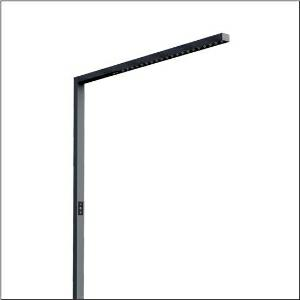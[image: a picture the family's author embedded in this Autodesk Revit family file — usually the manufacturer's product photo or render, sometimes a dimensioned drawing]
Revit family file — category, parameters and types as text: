
# Revit family: silica_31_floor_51my52fatcb
name_source: partatom
category: Lighting Fixtures
units: mm (PartAtom-declared; Revit-internal decimal feet)

## family parameters
Cut with Voids When Loaded = No
Host = Face
Light Source = No
Part Type = Normal
Room Calculation Point = No
Round Connector Dimension = Use Diameter
Shared = No

## types (1)
- --- (1 x LED, 8520 lm, 71 W, 4000K)
    Apparent Load = 71 VA
    CIE Flux Codes = 86 100 100 24 100
    Color Rendering = 80
    Color Temperature = 4000K
    Default Elevation = 1800 mm
    Description = Silica® 31 Floor, floorstanding luminaire, secondary optical cover: cover panel, of PMMA, light emission: direct/indirect distribution, primary light characteristic: symmetric, installation type: not mounted, LED, rated luminous flux: 8.520lm, luminous efficacy: 120lm/W, light colour: 8tw, colour temperature: 2700..6500K, control gear: Touchdim, daylight-dependent control, with cable with plug, mains connection: 230V, AC, 50Hz, connection cable included, cable length: 2,5m, rated input power: 71W, luminaire head, of aluminium, jet black (RAL 9005), length: 1.203mm, width: 52mm, supporting column, angular, of aluminium, jet black (RAL 9005), baseplate, of steel, jet black (RAL 9005), local control - self-sufficient standalone sensors, direct and indirect component separately switchable, protection rating (complete): IP20, insulation class (complete): insulation class I (protective earthing), certification: CE, ENEC, permissible operating ambient temperature: -20..+40°C, standard: EN 50419, packaging unit: 1 piece
    Height = 36 mm
    Lamp = 1 x LED
    Lamp Light Flux = 8520 lm
    Lamp Power = 71 W
    Lamp count = 1
    Length = 1203 mm
    Luminous efficacy = 120 lm/W
    Manufacturer = Siteco
    ModVariant = No
    Model = 51MY52FATCB
    Mounting Place = Floor
    Mounting Type = Freestanding
    Number of Poles = 1
    OnlyDefault = Yes
    Power Factor = 1
    Product Name = Silica 31 Floor
    Product group = floorstanding luminaire
    ProductGroupID = 1302
    Protection Class = Protection class I
    Protection Degree = IP 20
    RLX_Detail_Level = 1
    RLX_Emergency_Light_Flux = 0 lm
    RLX_Emergency_Type = 0
    RLX_Emergency_Type_DB = No
    RlxData = <blob elided: 20241 chars, md5=1c4d47be>
    Socket = socket
    Standby Power = 0 W
    System Light Flux = 8520 lm
    System Power = 71 W
    Type Comments = factory setting
    Type Image = l_1275297.jpg
    URL = http://relux.com
    VarID = @adj_087119
    Voltage = 0 V
    Weight = 0.00 kg
    Width = 52 mm  [stored 0.170604 ft]

note: [stored X ft] marks values corroborated as IEEE doubles in the binary element streams (Revit-internal decimal feet)

## geometry (parser evidence)
native form markers: Blend x4, Sweep x17
no freeform markers — native parametric forms only
